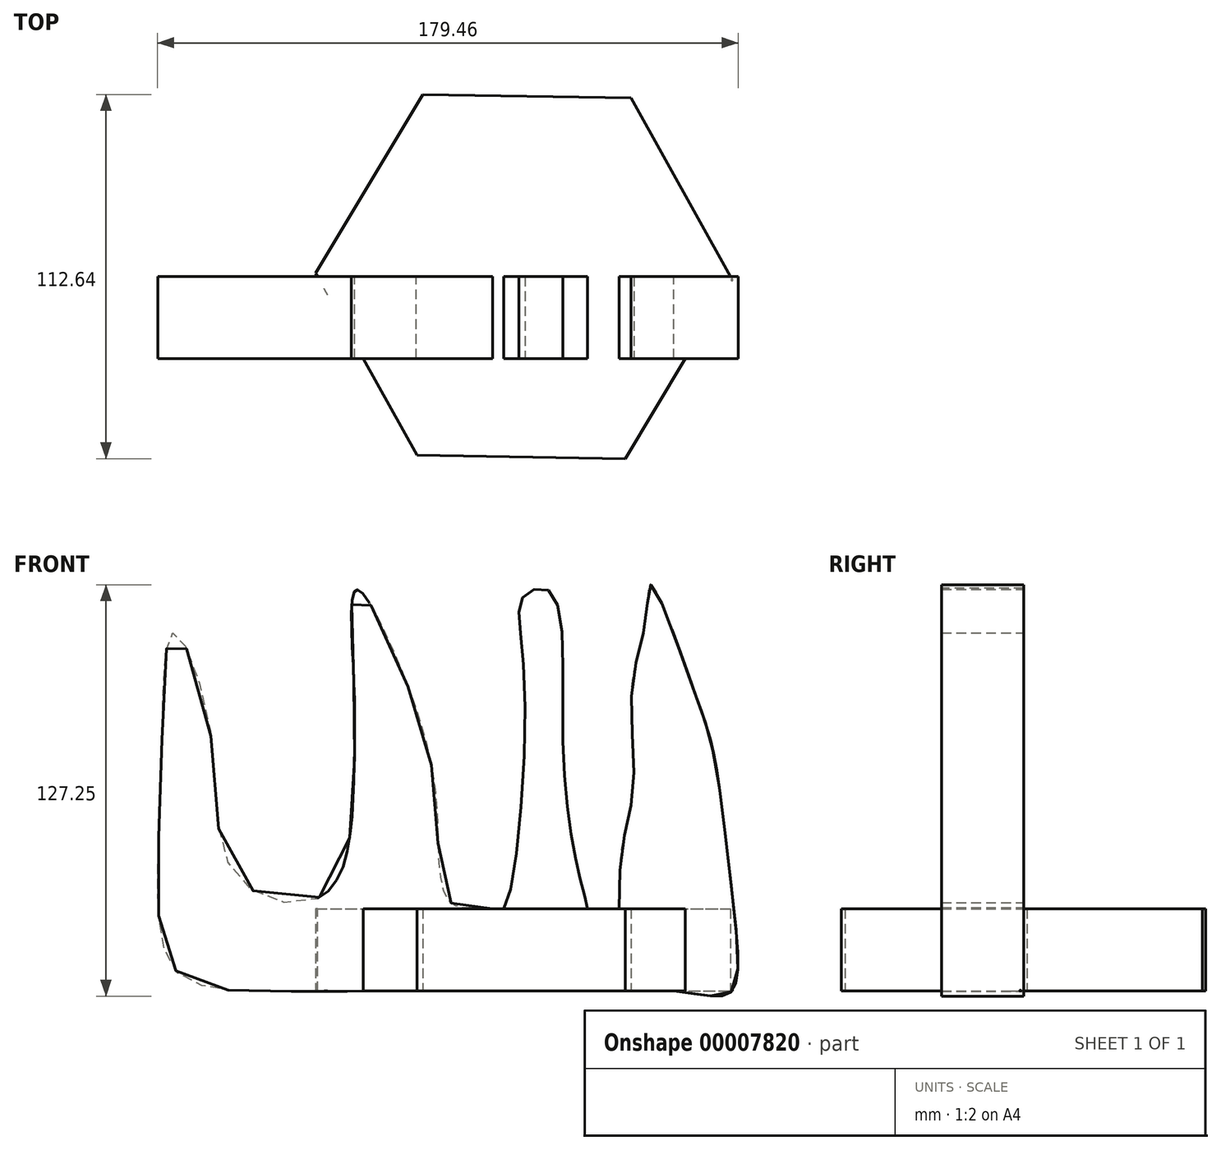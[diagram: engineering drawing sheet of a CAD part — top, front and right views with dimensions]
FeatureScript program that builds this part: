
annotation { "Feature Type Name" : "Feature", "Feature Type Description" : "" }
export const myFeature = defineFeature(function(context is Context, id is Id, definition is map)
    precondition{}
    {
        {
            var Q0;
            Q0=qCreatedBy(makeId("Top.planeOp"),FACE);
            var sketch = newSketch(context, id + "F0", { "sketchPlane" : qUnion([Q0])});
            skCircle(sketch, "E0.cCircle", {"center": v(0, 0) * mm, "radius": 55.81 * mm, "construction": true});
            skLineSegment(sketch, "E0.0", {"start": v(33.12, 55.29) * mm, "end": v(64.44, -1.04) * mm});
            skLineSegment(sketch, "E0.1", {"start": v(64.44, -1.04) * mm, "end": v(31.32, -56.32) * mm});
            skLineSegment(sketch, "E0.2", {"start": v(31.32, -56.32) * mm, "end": v(-33.12, -55.29) * mm});
            skLineSegment(sketch, "E0.3", {"start": v(-33.12, -55.29) * mm, "end": v(-64.44, 1.04) * mm});
            skLineSegment(sketch, "E0.4", {"start": v(-64.44, 1.04) * mm, "end": v(-31.32, 56.32) * mm});
            skLineSegment(sketch, "E0.5", {"start": v(-31.32, 56.32) * mm, "end": v(33.12, 55.29) * mm});
            skPoint(sketch, "E0.0.midPoint", {"position": v(48.78, 27.13) * mm});
            skSolve(sketch);
        }
        {
            var Q0;
            Q0 = qSketchRegion(id + "F0", true);
            extrude(context, id + "F1", {"entities" : qUnion([Q0]), "depth" : 25.4 * mm});
        }
        {
            var Q0;
            Q0=qCreatedBy(makeId("Front.planeOp"),FACE);
            var sketch = newSketch(context, id + "F2", { "sketchPlane" : qUnion([Q0])});
            skFitSpline(sketch, "E1", {"points": [v(-33.35, 0) * mm, v(-60.72, 0) * mm, v(-83.62, 0) * mm, v(-106.02, 4.73) * mm, v(-112.99, 24.14) * mm, v(-112, 73.42) * mm, v(-108.5, 110.75) * mm, v(-97.06, 80.88) * mm, v(-88.6, 35.1) * mm, v(-62.22, 29.62) * mm, v(-52.76, 61.97) * mm, v(-52.76, 99.8) * mm, v(-51.76, 124.19) * mm, v(-36.33, 95.32) * mm, v(-26.88, 55) * mm, v(-22.4, 27.13) * mm, v(-10.45, 25.63) * mm, v(-6.47, 25.14) * mm, v(0, 99.3) * mm, v(0, 122.2) * mm, v(7.96, 123.69) * mm, v(11.95, 81.88) * mm, v(15.93, 41.06) * mm, v(19.41, 26.63) * mm, v(21.4, 21.15) * mm, v(27.38, 18.17) * mm, v(29.86, 40.57) * mm, v(33.85, 62.96) * mm, v(33.35, 94.32) * mm, v(37.83, 115.72) * mm, v(39.32, 125.68) * mm, v(52.26, 93.82) * mm, v(58.73, 72.92) * mm, v(64.7, 26.63) * mm, v(64.2, 0) * mm, v(46.29, 0) * mm, v(-33.35, 0) * mm]});
            skSolve(sketch);
        }
        {
            var Q0;
            Q0 = qSketchRegion(id + "F2", true);
            extrude(context, id + "F3", {"entities" : qUnion([Q0]), "operationType" : NewBodyOperationType.ADD, "depth" : 25.4 * mm});
        }
    });
